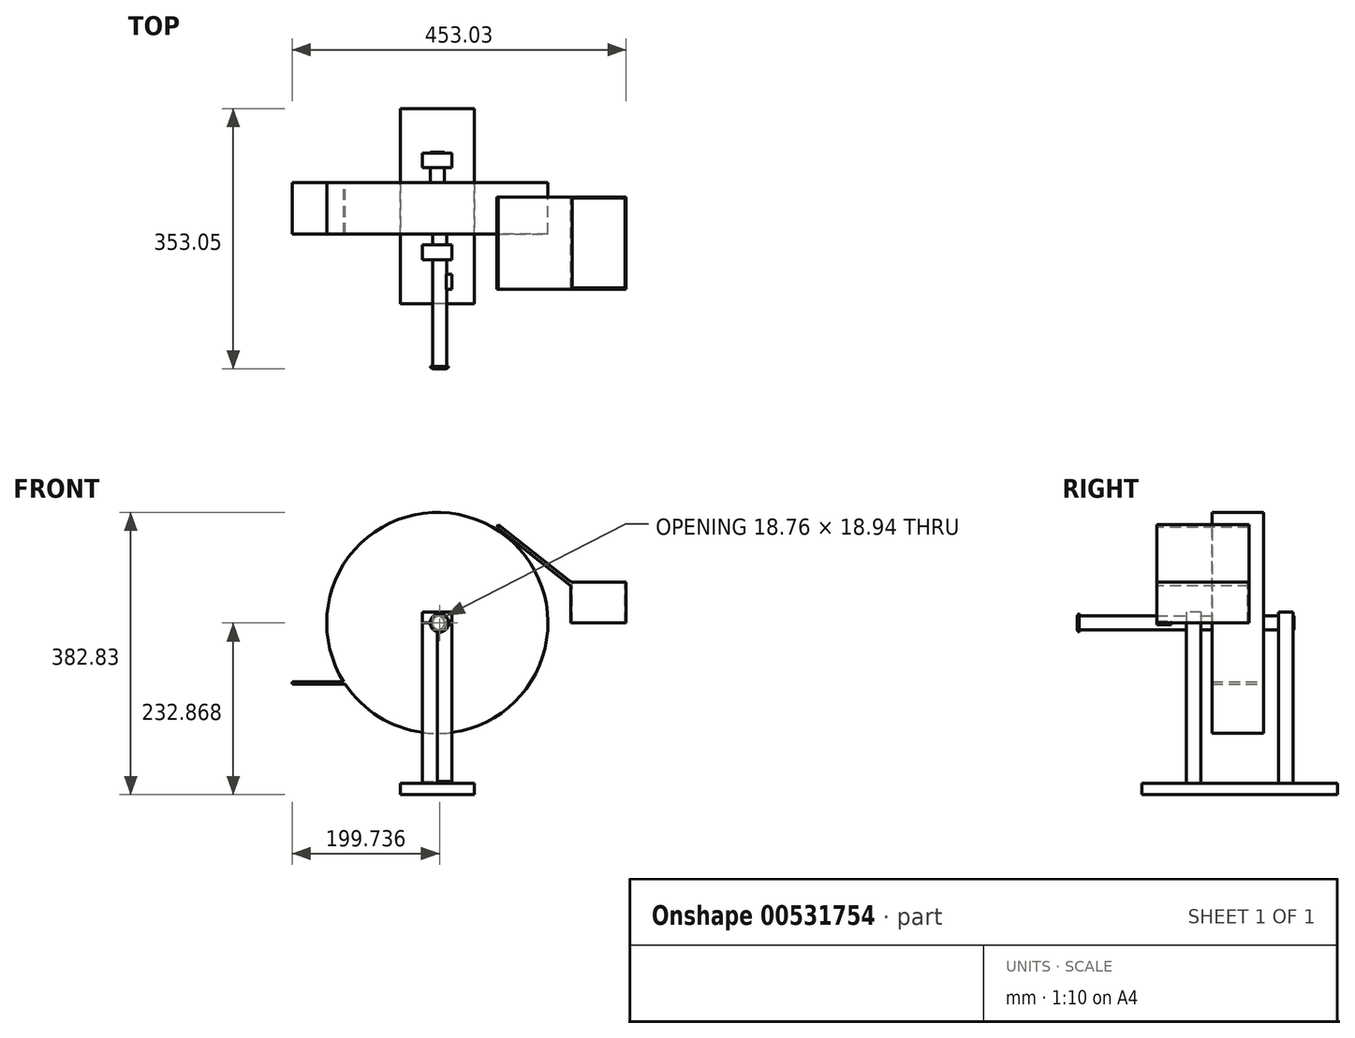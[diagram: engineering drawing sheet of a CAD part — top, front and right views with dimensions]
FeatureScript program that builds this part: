
annotation { "Feature Type Name" : "Feature", "Feature Type Description" : "" }
export const myFeature = defineFeature(function(context is Context, id is Id, definition is map)
    precondition{}
    {
        {
            var Q0;
            Q0=qCreatedBy(makeId("Front.planeOp"),FACE);
            var sketch = newSketch(context, id + "F0", { "sketchPlane" : qUnion([Q0])});
            skCircle(sketch, "E0", {"center": v(0, -0.07) * mm, "radius": 150 * mm});
            skSolve(sketch);
        }
        {
            var Q0;
            Q0 = qSketchRegion(id + "F0", true);
            extrude(context, id + "F1", {"entities" : qUnion([Q0]), "depth" : 70 * mm, "offsetDistance" : 25 * mm});
        }
        {
            var Q0;
            Q0=qCreatedBy(makeId("Right.planeOp"),FACE);
            var sketch = newSketch(context, id + "F2", { "sketchPlane" : qUnion([Q0])});
            skPoint(sketch, "E1.end.orphan", {"position": v(0, -80.23) * mm});
            skLineSegment(sketch, "E2", {"start": v(0, -80.23) * mm, "end": v(-70, -80.23) * mm});
            skLineSegment(sketch, "E3.top", {"start": v(0, -83.23) * mm, "end": v(-70, -83.23) * mm});
            skLineSegment(sketch, "E3.left", {"start": v(0, -80.23) * mm, "end": v(0, -83.23) * mm});
            skLineSegment(sketch, "E3.right", {"start": v(-70, -80.23) * mm, "end": v(-70, -83.23) * mm});
            skLineSegment(sketch, "E4", {"start": v(0, 0) * mm, "end": v(0, -80.23) * mm});
            skSolve(sketch);
        }
        {
            var Q0;
            Q0 = qSketchRegion(id + "F2", true);
            extrude(context, id + "F3", {"entities" : qUnion([Q0]), "operationType" : NewBodyOperationType.ADD, "oppositeDirection" : true, "depth" : 196.78 * mm, "offsetDistance" : 25 * mm});
        }
        {
            var Q0;
            Q0=makeQuery(id+"F3.boolean.opBoolean","MERGE",FACE,{"derivedFrom":[makeQuery(id+"F1.opExtrude","CAP_FACE",FACE,{"disambiguationData":[OSD([sQuery(id+"F0.wireOp",EDGE,"E0")])],"isStart":false}),makeQuery(id+"F3.opExtrude","SWEPT_FACE",FACE,{"disambiguationData":[OSD([sQuery(id+"F2.wireOp",EDGE,"E3.right")])]})]});
            var sketch = newSketch(context, id + "F4", { "sketchPlane" : qUnion([Q0])});
            skSolve(sketch);
        }
        {
            var Q0;
            {var subQ0=sQuery(id+"F2.wireOp",EDGE,"E3.right");Q0=makeQuery(id+"F4.imprint","IMPRINT",FACE,{"disambiguationData":[TD([[makeQuery(id+"F4.imprint","IMPRINT",EDGE,{"derivedFrom":makeQuery(id+"F3.opExtrude","CAP_EDGE",EDGE,{"disambiguationData":[OSD([subQ0])],"isStart":false})}),1.0]])]});}
            var sketch = newSketch(context, id + "F5", { "sketchPlane" : qUnion([Q0])});
            skCircle(sketch, "E5", {"center": v(2.96, 0) * mm, "radius": 9.5 * mm});
            skSolve(sketch);
        }
        {
            var Q0;
            Q0 = qSketchRegion(id + "F5", true);
            extrude(context, id + "F6", {"entities" : qUnion([Q0]), "operationType" : NewBodyOperationType.ADD, "depth" : 180 * mm, "offsetDistance" : 25 * mm});
        }
        {
            var Q0;
            Q0=makeQuery(id+"F3.boolean.opBoolean","MERGE",FACE,{"derivedFrom":[makeQuery(id+"F1.opExtrude","CAP_FACE",FACE,{"disambiguationData":[OSD([sQuery(id+"F0.wireOp",EDGE,"E0")])],"isStart":true}),makeQuery(id+"F3.opExtrude","SWEPT_FACE",FACE,{"disambiguationData":[OSD([sQuery(id+"F2.wireOp",EDGE,"E3.left")])]})]});
            var sketch = newSketch(context, id + "F7", { "sketchPlane" : qUnion([Q0])});
            skCircle(sketch, "E6", {"center": v(0, 0) * mm, "radius": 9.5 * mm});
            skSolve(sketch);
        }
        {
            var Q0;
            Q0=makeQuery(id+"F7.imprint","IMPRINT",FACE,{"disambiguationData":[TD([[makeQuery(id+"F7.imprint","IMPRINT",EDGE,{"derivedFrom":sQuery(id+"F7.wireOp",EDGE,"E6")}),1.0]])]});
            extrude(context, id + "F8", {"entities" : qUnion([Q0]), "operationType" : NewBodyOperationType.ADD, "depth" : 40 * mm, "offsetDistance" : 25 * mm});
        }
        {
            var Q0;
            Q0=qCreatedBy(makeId("Right.planeOp"),FACE);
            var sketch = newSketch(context, id + "F9", { "sketchPlane" : qUnion([Q0])});
            skLineSegment(sketch, "E7", {"start": v(0, 9.5) * mm, "end": v(40, 9.5) * mm});
            skLineSegment(sketch, "E8.bottom", {"start": v(40, 9.5) * mm, "end": v(20, 9.5) * mm});
            skLineSegment(sketch, "E8.top", {"start": v(40, -205.5) * mm, "end": v(20, -205.5) * mm});
            skLineSegment(sketch, "E8.left", {"start": v(40, 9.5) * mm, "end": v(40, -205.5) * mm});
            skLineSegment(sketch, "E8.right", {"start": v(20, 9.5) * mm, "end": v(20, -205.5) * mm});
            skSolve(sketch);
        }
        {
            var Q0;
            Q0 = qSketchRegion(id + "F9", true);
            extrude(context, id + "F10", {"entities" : qUnion([Q0]), "operationType" : NewBodyOperationType.ADD, "oppositeDirection" : true, "depth" : 20 * mm, "offsetDistance" : 25 * mm});
        }
        {
            var Q0;
            Q0=makeQuery(id+"F10.opExtrude","CAP_FACE",FACE,{"disambiguationData":[OSD([sQuery(id+"F9.wireOp",EDGE,"E8.bottom"),sQuery(id+"F9.wireOp",EDGE,"E8.top"),sQuery(id+"F9.wireOp",EDGE,"E8.left"),sQuery(id+"F9.wireOp",EDGE,"E8.right")])],"isStart":true});
            var sketch = newSketch(context, id + "F11", { "sketchPlane" : qUnion([Q0])});
            skLineSegment(sketch, "E9.bottom", {"start": v(40, -205.5) * mm, "end": v(20, -205.5) * mm});
            skLineSegment(sketch, "E9.top", {"start": v(40, 9.5) * mm, "end": v(20, 9.5) * mm});
            skLineSegment(sketch, "E9.left", {"start": v(40, -205.5) * mm, "end": v(40, 9.5) * mm});
            skLineSegment(sketch, "E9.right", {"start": v(20, -205.5) * mm, "end": v(20, 9.5) * mm});
            skSolve(sketch);
        }
        {
            var Q0;
            {var subQ0=sQuery(id+"F11.wireOp",EDGE,"E9.top");Q0=makeQuery(id+"F11.imprint","IMPRINT",FACE,{"disambiguationData":[TD([[makeQuery(id+"F11.imprint","IMPRINT",EDGE,{"derivedFrom":subQ0}),1.0]])]});}
            var Q1;
            {var subQ0=sQuery(id+"F11.wireOp",EDGE,"E9.bottom");Q1=makeQuery(id+"F11.imprint","IMPRINT",FACE,{"disambiguationData":[TD([[makeQuery(id+"F11.imprint","IMPRINT",EDGE,{"derivedFrom":subQ0}),-1.0]])]});}
            extrude(context, id + "F12", {"entities" : qUnion([Q0, Q1]), "operationType" : NewBodyOperationType.ADD, "depth" : 20 * mm, "offsetDistance" : 25 * mm});
        }
        {
            var Q0;
            Q0=qCreatedBy(makeId("Top.planeOp"),FACE);
            var sketch = newSketch(context, id + "F13", { "sketchPlane" : qUnion([Q0])});
            skLineSegment(sketch, "E10", {"start": v(0, 0) * mm, "end": v(0, 40) * mm});
            skLineSegment(sketch, "E11", {"start": v(0, 40) * mm, "end": v(-20, 40) * mm});
            skLineSegment(sketch, "E12.bottom", {"start": v(-20, 40) * mm, "end": v(20, 40) * mm});
            skLineSegment(sketch, "E12.top", {"start": v(-20, 20) * mm, "end": v(20, 20) * mm});
            skLineSegment(sketch, "E12.left", {"start": v(-20, 40) * mm, "end": v(-20, 20) * mm});
            skLineSegment(sketch, "E12.right", {"start": v(20, 40) * mm, "end": v(20, 20) * mm});
            skSolve(sketch);
        }
        {
            var Q0;
            Q0 = qSketchRegion(id + "F13", true);
            extrude(context, id + "F14", {"entities" : qUnion([Q0]), "operationType" : NewBodyOperationType.ADD, "depth" : 15 * mm, "offsetDistance" : 25 * mm});
        }
        {
            var Q0;
            Q0=makeQuery(id+"F12.boolean.opBoolean","MERGE",FACE,{"derivedFrom":[makeQuery(id+"F10.opExtrude","SWEPT_FACE",FACE,{"disambiguationData":[OSD([sQuery(id+"F9.wireOp",EDGE,"E8.top")])]}),makeQuery(id+"F12.opExtrude","SWEPT_FACE",FACE,{"disambiguationData":[OSD([sQuery(id+"F11.wireOp",EDGE,"E9.bottom")])]})]});
            var sketch = newSketch(context, id + "F15", { "sketchPlane" : qUnion([Q0])});
            skLineSegment(sketch, "E13.bottom", {"start": v(-20, -20) * mm, "end": v(20, -20) * mm});
            skLineSegment(sketch, "E13.top", {"start": v(-20, -40) * mm, "end": v(20, -40) * mm});
            skLineSegment(sketch, "E13.left", {"start": v(-20, -20) * mm, "end": v(-20, -40) * mm});
            skLineSegment(sketch, "E13.right", {"start": v(20, -20) * mm, "end": v(20, -40) * mm});
            skSolve(sketch);
        }
        {
            var Q0;
            Q0 = qSketchRegion(id + "F15", true);
            extrude(context, id + "F16", {"entities" : qUnion([Q0]), "operationType" : NewBodyOperationType.ADD, "depth" : 25 * mm, "offsetDistance" : 25 * mm});
        }
        {
            var Q0;
            Q0=qCreatedBy(makeId("Right.planeOp"),FACE);
            var sketch = newSketch(context, id + "F17", { "sketchPlane" : qUnion([Q0])});
            skLineSegment(sketch, "E14.bottom", {"start": v(-85, 0) * mm, "end": v(-105, 0) * mm});
            skLineSegment(sketch, "E14.top", {"start": v(-85, -215) * mm, "end": v(-105, -215) * mm});
            skLineSegment(sketch, "E14.left", {"start": v(-85, 0) * mm, "end": v(-85, -215) * mm});
            skLineSegment(sketch, "E14.right", {"start": v(-105, 0) * mm, "end": v(-105, -215) * mm});
            skLineSegment(sketch, "E15", {"start": v(-85, 15) * mm, "end": v(-105, 15) * mm});
            skLineSegment(sketch, "E16.left", {"start": v(-85, 0) * mm, "end": v(-85, 15) * mm});
            skLineSegment(sketch, "E16.right", {"start": v(-105, 0) * mm, "end": v(-105, 15) * mm});
            skSolve(sketch);
        }
        {
            var Q0;
            Q0 = qSketchRegion(id + "F17", true);
            extrude(context, id + "F18", {"entities" : qUnion([Q0]), "operationType" : NewBodyOperationType.ADD, "depth" : 20 * mm, "offsetDistance" : 25 * mm});
        }
        {
            var Q0;
            Q0=qCreatedBy(makeId("Top.planeOp"),FACE);
            var sketch = newSketch(context, id + "F19", { "sketchPlane" : qUnion([Q0])});
            skLineSegment(sketch, "E17", {"start": v(0, -84.96) * mm, "end": v(0, -104.96) * mm});
            skLineSegment(sketch, "E18.bottom", {"start": v(0, -84.96) * mm, "end": v(-20, -84.96) * mm});
            skLineSegment(sketch, "E18.top", {"start": v(0, -104.96) * mm, "end": v(-20, -104.96) * mm});
            skLineSegment(sketch, "E18.right", {"start": v(-20, -84.96) * mm, "end": v(-20, -104.96) * mm});
            skSolve(sketch);
        }
        {
            var Q0;
            Q0 = qSketchRegion(id + "F19", true);
            extrude(context, id + "F20", {"entities" : qUnion([Q0]), "operationType" : NewBodyOperationType.ADD, "depth" : 15 * mm, "offsetDistance" : 25 * mm});
        }
        {
            var Q0;
            Q0=qCreatedBy(makeId("Top.planeOp"),FACE);
            var sketch = newSketch(context, id + "F21", { "sketchPlane" : qUnion([Q0])});
            skLineSegment(sketch, "E19", {"start": v(0, 0) * mm, "end": v(0, -84.98) * mm});
            skLineSegment(sketch, "E20.bottom", {"start": v(0, -84.98) * mm, "end": v(-20, -84.98) * mm});
            skLineSegment(sketch, "E20.top", {"start": v(0, -104.98) * mm, "end": v(-20, -104.98) * mm});
            skLineSegment(sketch, "E20.left", {"start": v(0, -84.98) * mm, "end": v(0, -104.98) * mm});
            skLineSegment(sketch, "E20.right", {"start": v(-20, -84.98) * mm, "end": v(-20, -104.98) * mm});
            skSolve(sketch);
        }
        {
            var Q0;
            Q0 = qSketchRegion(id + "F21", true);
            extrude(context, id + "F22", {"entities" : qUnion([Q0]), "operationType" : NewBodyOperationType.ADD, "oppositeDirection" : true, "depth" : 215 * mm, "offsetDistance" : 25 * mm});
        }
        {
            var Q0;
            Q0=makeQuery(id+"F22.boolean.opBoolean","MERGE",FACE,{"derivedFrom":[makeQuery(id+"F18.opExtrude","SWEPT_FACE",FACE,{"disambiguationData":[OSD([sQuery(id+"F17.wireOp",EDGE,"E14.top")])]}),makeQuery(id+"F22.opExtrude","CAP_FACE",FACE,{"disambiguationData":[OSD([sQuery(id+"F21.wireOp",EDGE,"E20.bottom"),sQuery(id+"F21.wireOp",EDGE,"E20.top"),sQuery(id+"F21.wireOp",EDGE,"E20.left"),sQuery(id+"F21.wireOp",EDGE,"E20.right")])],"isStart":false})]});
            var sketch = newSketch(context, id + "F23", { "sketchPlane" : qUnion([Q0])});
            skLineSegment(sketch, "E21.bottom", {"start": v(-20, 104.98) * mm, "end": v(20, 104.98) * mm});
            skLineSegment(sketch, "E21.top", {"start": v(-20, 85) * mm, "end": v(20, 85) * mm});
            skLineSegment(sketch, "E21.left", {"start": v(-20, 104.98) * mm, "end": v(-20, 85) * mm});
            skLineSegment(sketch, "E21.right", {"start": v(20, 104.98) * mm, "end": v(20, 85) * mm});
            skSolve(sketch);
        }
        {
            var Q0;
            Q0 = qSketchRegion(id + "F23", true);
            extrude(context, id + "F24", {"entities" : qUnion([Q0]), "operationType" : NewBodyOperationType.ADD, "depth" : 15.5 * mm, "offsetDistance" : 25 * mm});
        }
        {
            var Q0;
            Q0=qCreatedBy(makeId("Right.planeOp"),FACE);
            var sketch = newSketch(context, id + "F25", { "sketchPlane" : qUnion([Q0])});
            skLineSegment(sketch, "E22", {"start": v(40.05, -217.9) * mm, "end": v(40, -217.9) * mm});
            skLineSegment(sketch, "E23", {"start": v(40.05, -217.9) * mm, "end": v(100.05, -217.9) * mm});
            skLineSegment(sketch, "E24", {"start": v(100.05, -217.9) * mm, "end": v(100.05, -232.9) * mm});
            skLineSegment(sketch, "E25", {"start": v(100.05, -232.9) * mm, "end": v(-126.08, -232.9) * mm});
            skLineSegment(sketch, "E26", {"start": v(40.05, -217.9) * mm, "end": v(-141.98, -217.9) * mm});
            skLineSegment(sketch, "E27", {"start": v(100.05, -217.9) * mm, "end": v(-164.95, -217.9) * mm});
            skLineSegment(sketch, "E28", {"start": v(-164.95, -217.9) * mm, "end": v(-164.95, -232.9) * mm});
            skLineSegment(sketch, "E29", {"start": v(-164.95, -232.9) * mm, "end": v(-126.08, -232.9) * mm});
            skLineSegment(sketch, "E30", {"start": v(40.05, -217.9) * mm, "end": v(40, -230.5) * mm});
            skLineSegment(sketch, "E31", {"start": v(40, -230.5) * mm, "end": v(40, -232.9) * mm});
            skLineSegment(sketch, "E32", {"start": v(20, -232.9) * mm, "end": v(20, -230.5) * mm});
            skSolve(sketch);
        }
        {
            var Q0;
            Q0 = qSketchRegion(id + "F25", true);
            extrude(context, id + "F26", {"entities" : qUnion([Q0]), "operationType" : NewBodyOperationType.ADD, "depth" : 50 * mm, "offsetDistance" : 25 * mm});
        }
        {
            var Q0;
            Q0=makeQuery(id+"F26.opExtrude","CAP_FACE",FACE,{"disambiguationData":[OSD([sQuery(id+"F25.wireOp",EDGE,"E24"),sQuery(id+"F25.wireOp",EDGE,"E25"),sQuery(id+"F25.wireOp",EDGE,"E27"),sQuery(id+"F25.wireOp",EDGE,"E28"),sQuery(id+"F25.wireOp",EDGE,"E29")])],"isStart":true});
            var sketch = newSketch(context, id + "F27", { "sketchPlane" : qUnion([Q0])});
            skLineSegment(sketch, "E33.bottom", {"start": v(-100.05, -217.9) * mm, "end": v(164.95, -217.9) * mm});
            skLineSegment(sketch, "E33.top", {"start": v(-100.05, -232.9) * mm, "end": v(164.95, -232.9) * mm});
            skLineSegment(sketch, "E33.left", {"start": v(-100.05, -217.9) * mm, "end": v(-100.05, -232.9) * mm});
            skLineSegment(sketch, "E33.right", {"start": v(164.95, -217.9) * mm, "end": v(164.95, -232.9) * mm});
            skLineSegment(sketch, "E34", {"start": v(-40, -230.5) * mm, "end": v(-40, -232.9) * mm});
            skSolve(sketch);
        }
        {
            var Q0;
            Q0 = qSketchRegion(id + "F27", true);
            extrude(context, id + "F28", {"entities" : qUnion([Q0]), "operationType" : NewBodyOperationType.ADD, "depth" : 50 * mm, "offsetDistance" : 25 * mm});
        }
        {
            var Q0;
            Q0=qCreatedBy(makeId("Right.planeOp"),FACE);
            var sketch = newSketch(context, id + "F29", { "sketchPlane" : qUnion([Q0])});
            skLineSegment(sketch, "E35", {"start": v(0, 0) * mm, "end": v(-135, 0) * mm});
            skLineSegment(sketch, "E36.bottom", {"start": v(-145, -2.5) * mm, "end": v(-125, -2.5) * mm});
            skLineSegment(sketch, "E36.top", {"start": v(-145, 2.5) * mm, "end": v(-125, 2.5) * mm});
            skLineSegment(sketch, "E36.left", {"start": v(-145, -2.5) * mm, "end": v(-145, 2.5) * mm});
            skLineSegment(sketch, "E36.right", {"start": v(-125, -2.5) * mm, "end": v(-125, 2.5) * mm});
            skPoint(sketch, "E36.middle", {"position": v(-135, 0) * mm});
            skLineSegment(sketch, "E37", {"start": v(0, 0) * mm, "end": v(-125, 0) * mm});
            skSolve(sketch);
        }
        {
            var Q0;
            Q0 = qSketchRegion(id + "F29", true);
            extrude(context, id + "F30", {"entities" : qUnion([Q0]), "operationType" : NewBodyOperationType.ADD, "oppositeDirection" : true, "depth" : 60 * mm, "offsetDistance" : 25 * mm});
        }
        {
            var Q0;
            Q0 = qSketchRegion(id + "F29", true);
            extrude(context, id + "F31", {"entities" : qUnion([Q0]), "operationType" : NewBodyOperationType.ADD, "depth" : 20 * mm, "offsetDistance" : 25 * mm});
        }
        {
            var Q0;
            Q0=makeQuery(id+"F3.boolean.opBoolean","MERGE",FACE,{"derivedFrom":[makeQuery(id+"F1.opExtrude","CAP_FACE",FACE,{"disambiguationData":[OSD([sQuery(id+"F0.wireOp",EDGE,"E0")])],"isStart":true}),makeQuery(id+"F3.opExtrude","SWEPT_FACE",FACE,{"disambiguationData":[OSD([sQuery(id+"F2.wireOp",EDGE,"E3.left")])]})]});
            cPlane(context, id + "F32", {"entities" : qUnion([Q0]), "cplaneType" : CPlaneType.OFFSET, "offset" : 125 * mm, "oppositeDirection" : true, "width" : 150 * mm, "height" : 150 * mm});
        }
        {
            var Q0;
            Q0=qCreatedBy(id+"F32.planeOp",FACE);
            var sketch = newSketch(context, id + "F33", { "sketchPlane" : qUnion([Q0])});
            skLineSegment(sketch, "E38", {"start": v(0, 0) * mm, "end": v(-20, 0) * mm});
            skLineSegment(sketch, "E39", {"start": v(-20, 0) * mm, "end": v(-20, 2.5) * mm});
            skLineSegment(sketch, "E40", {"start": v(-20, 2.5) * mm, "end": v(-20, 0) * mm});
            skLineSegment(sketch, "E41", {"start": v(-20, 0) * mm, "end": v(-20, -2.5) * mm});
            skLineSegment(sketch, "E42", {"start": v(-181.25, 0) * mm, "end": v(-181.25, 55.52) * mm});
            skLineSegment(sketch, "E43", {"start": v(-181.25, 0) * mm, "end": v(-256.25, 0) * mm});
            skLineSegment(sketch, "E44", {"start": v(-256.25, 0) * mm, "end": v(-256.25, 55.52) * mm});
            skLineSegment(sketch, "E45", {"start": v(-256.25, 55.52) * mm, "end": v(-181.25, 55.52) * mm});
            skPoint(sketch, "E46.start.orphan", {"position": v(-80.39, 124.36) * mm});
            skPoint(sketch, "E47.end.orphan", {"position": v(-80.39, 129.36) * mm});
            skLineSegment(sketch, "E48", {"start": v(-20, 2.5) * mm, "end": v(-82.34, 133.41) * mm});
            skLineSegment(sketch, "E49", {"start": v(-82.34, 133.41) * mm, "end": v(-181.25, 55.52) * mm});
            skLineSegment(sketch, "E50", {"start": v(-20, -2.5) * mm, "end": v(-82.34, 128.41) * mm});
            skLineSegment(sketch, "E51", {"start": v(-82.34, 128.41) * mm, "end": v(-181.25, 50.52) * mm});
            skLineSegment(sketch, "E52", {"start": v(-20, 2.5) * mm, "end": v(-20, 133.41) * mm});
            skLineSegment(sketch, "E53", {"start": v(-20, 133.41) * mm, "end": v(-82.34, 133.41) * mm});
            skSolve(sketch);
        }
        {
            var Q0;
            Q0=makeQuery(id+"F33.imprint","IMPRINT",FACE,{"disambiguationData":[TD([[makeQuery(id+"F33.imprint","IMPRINT",EDGE,{"derivedFrom":sQuery(id+"F33.wireOp",EDGE,"E40")}),-1.0]])]});
            var Q1;
            {var subQ0=sQuery(id+"F33.wireOp",EDGE,"E43");Q1=makeQuery(id+"F33.imprint","IMPRINT",FACE,{"disambiguationData":[TD([[makeQuery(id+"F33.imprint","IMPRINT",EDGE,{"derivedFrom":subQ0}),-1.0]])]});}
            extrude(context, id + "F34", {"entities" : qUnion([Q0, Q1]), "oppositeDirection" : true, "depth" : 20 * mm, "offsetDistance" : 25 * mm});
        }
        {
            var Q0;
            Q0=makeQuery(id+"F34.opExtrude","CAP_FACE",FACE,{"disambiguationData":[OSD([sQuery(id+"F33.wireOp",EDGE,"E40"),sQuery(id+"F33.wireOp",EDGE,"E41"),sQuery(id+"F33.wireOp",EDGE,"E42"),sQuery(id+"F33.wireOp",EDGE,"E43"),sQuery(id+"F33.wireOp",EDGE,"E44"),sQuery(id+"F33.wireOp",EDGE,"E45"),sQuery(id+"F33.wireOp",EDGE,"E48"),sQuery(id+"F33.wireOp",EDGE,"E49"),sQuery(id+"F33.wireOp",EDGE,"E50"),sQuery(id+"F33.wireOp",EDGE,"E51")])],"isStart":false});
            var sketch = newSketch(context, id + "F35", { "sketchPlane" : qUnion([Q0])});
            skLineSegment(sketch, "E54", {"start": v(82.34, 128.41) * mm, "end": v(80.6, 129.78) * mm});
            skLineSegment(sketch, "E55", {"start": v(80.6, 129.78) * mm, "end": v(82.34, 133.41) * mm});
            skLineSegment(sketch, "E56", {"start": v(82.34, 133.41) * mm, "end": v(181.25, 55.52) * mm});
            skLineSegment(sketch, "E57", {"start": v(181.25, 55.52) * mm, "end": v(181.25, 50.52) * mm});
            skLineSegment(sketch, "E58", {"start": v(181.25, 50.52) * mm, "end": v(82.34, 128.41) * mm});
            skSolve(sketch);
        }
        {
            var Q0;
            Q0 = qSketchRegion(id + "F35", true);
            extrude(context, id + "F36", {"entities" : qUnion([Q0]), "operationType" : NewBodyOperationType.ADD, "oppositeDirection" : true, "depth" : 125 * mm, "offsetDistance" : 25 * mm});
        }
        {
            var Q0;
            {var subQ0=sQuery(id+"F33.wireOp",EDGE,"E45");var subQ1=sQuery(id+"F33.wireOp",EDGE,"E44");var subQ2=sQuery(id+"F33.wireOp",EDGE,"E43");var subQ3=sQuery(id+"F33.wireOp",EDGE,"E42");var subQ4=sQuery(id+"F33.wireOp",EDGE,"E49");var subQ5=sQuery(id+"F33.wireOp",EDGE,"E51");Q0=makeQuery(id+"F36.boolean.opBoolean","SPLIT",FACE,{"disambiguationData":[TD([makeQuery(id+"F34.opExtrude","SWEPT_FACE",FACE,{"disambiguationData":[OSD([subQ3])]})])],"derivedFrom":makeQuery(id+"F34.opExtrude","CAP_FACE",FACE,{"disambiguationData":[OSD([sQuery(id+"F33.wireOp",EDGE,"E40"),sQuery(id+"F33.wireOp",EDGE,"E41"),subQ3,subQ2,subQ1,subQ0,sQuery(id+"F33.wireOp",EDGE,"E48"),subQ4,sQuery(id+"F33.wireOp",EDGE,"E50"),subQ5])],"isStart":true})});}
            extrude(context, id + "F37", {"entities" : qUnion([Q0]), "operationType" : NewBodyOperationType.ADD, "depth" : 105 * mm, "offsetDistance" : 25 * mm});
        }
        {
            var Q0;
            {var subQ0=sQuery(id+"F33.wireOp",EDGE,"E45");Q0=makeQuery(id+"F37.boolean.opBoolean","MERGE",FACE,{"derivedFrom":[makeQuery(id+"F34.opExtrude","SWEPT_FACE",FACE,{"disambiguationData":[OSD([subQ0])]}),makeQuery(id+"F37.opExtrude","SWEPT_FACE",FACE,{"disambiguationData":[OSD([subQ0])]})]});}
            var sketch = newSketch(context, id + "F38", { "sketchPlane" : qUnion([Q0])});
            skLineSegment(sketch, "E59.bottom", {"start": v(254.75, -143.5) * mm, "end": v(182.75, -143.5) * mm});
            skLineSegment(sketch, "E59.top", {"start": v(254.75, -21.5) * mm, "end": v(182.75, -21.5) * mm});
            skLineSegment(sketch, "E59.left", {"start": v(254.75, -143.5) * mm, "end": v(254.75, -21.5) * mm});
            skLineSegment(sketch, "E59.right", {"start": v(182.75, -143.5) * mm, "end": v(182.75, -21.5) * mm});
            skPoint(sketch, "E59.middle", {"position": v(218.75, -82.5) * mm});
            skPoint(sketch, "E59.middle.positionSnap0", {"position": v(256.25, -82.5) * mm});
            skPoint(sketch, "E59.middle.positionSnap1", {"position": v(218.75, -20) * mm});
            skPoint(sketch, "E59.centerSnap0", {"position": v(256.25, -82.5) * mm});
            skPoint(sketch, "E59.centerSnap1", {"position": v(218.75, -20) * mm});
            skSolve(sketch);
        }
        {
            var Q0;
            Q0 = qSketchRegion(id + "F38", true);
            var Q1;
            Q1=makeQuery(id+"F30.opExtrude","SWEPT_FACE",FACE,{"disambiguationData":[OSD([sQuery(id+"F29.wireOp",EDGE,"E36.top")])]});
            extrude(context, id + "F39", {"entities" : qUnion([Q0, Q1]), "operationType" : NewBodyOperationType.REMOVE, "oppositeDirection" : true, "depth" : 161 * mm, "offsetDistance" : 25 * mm});
        }
        {
            var Q0;
            Q0=makeQuery(id+"F6.opExtrude","CAP_FACE",FACE,{"disambiguationData":[OSD([sQuery(id+"F5.wireOp",EDGE,"E5")])],"isStart":false});
            var sketch = newSketch(context, id + "F40", { "sketchPlane" : qUnion([Q0])});
            skCircle(sketch, "E60", {"center": v(2.96, 0) * mm, "radius": 12.5 * mm});
            skSolve(sketch);
        }
        {
            var Q0;
            Q0 = qSketchRegion(id + "F40", true);
            extrude(context, id + "F41", {"entities" : qUnion([Q0]), "operationType" : NewBodyOperationType.ADD, "depth" : 3 * mm, "offsetDistance" : 25 * mm});
        }
        {
            var Q0;
            Q0=makeQuery(id+"F41.opExtrude","CAP_EDGE",EDGE,{"disambiguationData":[OSD([sQuery(id+"F40.wireOp",EDGE,"E60")])],"isStart":false});
            fillet(context, id + "F42", {"entities" : qUnion([Q0]), "radius" : 5 * mm, "tangentPropagation" : true, "allowEdgeOverflow" : false});
        }
        {
            var Q0;
            Q0=makeQuery(id+"F16.boolean.opBoolean","MERGE",FACE,{"derivedFrom":[makeQuery(id+"F14.boolean.opBoolean","MERGE",FACE,{"derivedFrom":[makeQuery(id+"F12.boolean.opBoolean","MERGE",FACE,{"derivedFrom":[makeQuery(id+"F10.boolean.opBoolean","MERGE",FACE,{"derivedFrom":[makeQuery(id+"F8.opExtrude","CAP_FACE",FACE,{"disambiguationData":[OSD([sQuery(id+"F7.wireOp",EDGE,"E6")])],"isStart":false}),makeQuery(id+"F10.opExtrude","SWEPT_FACE",FACE,{"disambiguationData":[OSD([sQuery(id+"F9.wireOp",EDGE,"E8.left")])]})]}),makeQuery(id+"F12.opExtrude","SWEPT_FACE",FACE,{"disambiguationData":[OSD([sQuery(id+"F11.wireOp",EDGE,"E9.left")])]})]}),makeQuery(id+"F14.opExtrude","SWEPT_FACE",FACE,{"disambiguationData":[OSD([sQuery(id+"F13.wireOp",EDGE,"E12.bottom")])]})]}),makeQuery(id+"F16.opExtrude","SWEPT_FACE",FACE,{"disambiguationData":[OSD([sQuery(id+"F15.wireOp",EDGE,"E13.top")])]})]});
            var sketch = newSketch(context, id + "F43", { "sketchPlane" : qUnion([Q0])});
            skCircle(sketch, "E61", {"center": v(0, 0) * mm, "radius": 9.5 * mm});
            skSolve(sketch);
        }
        {
            var Q0;
            Q0 = qSketchRegion(id + "F43", true);
            extrude(context, id + "F44", {"entities" : qUnion([Q0]), "operationType" : NewBodyOperationType.ADD, "depth" : 1 * mm, "offsetDistance" : 25 * mm});
        }
        {
            var Q0;
            Q0=makeQuery(id+"F36.boolean.opBoolean","MERGE",EDGE,{"derivedFrom":[makeQuery(id+"F34.opExtrude","SWEPT_EDGE",EDGE,{"disambiguationData":[OSD([sQuery(id+"F33.wireOp",EDGE,"E48"),sQuery(id+"F33.wireOp",EDGE,"E49"),sQuery(id+"F33.wireOp",EDGE,"E53")])]}),makeQuery(id+"F36.opExtrude","SWEPT_EDGE",EDGE,{"disambiguationData":[OSD([sQuery(id+"F35.wireOp",EDGE,"E55"),sQuery(id+"F35.wireOp",EDGE,"E56")])]})]});
            fillet(context, id + "F45", {"entities" : qUnion([Q0]), "radius" : 7.64 * mm, "tangentPropagation" : true, "allowEdgeOverflow" : false});
        }
    });
